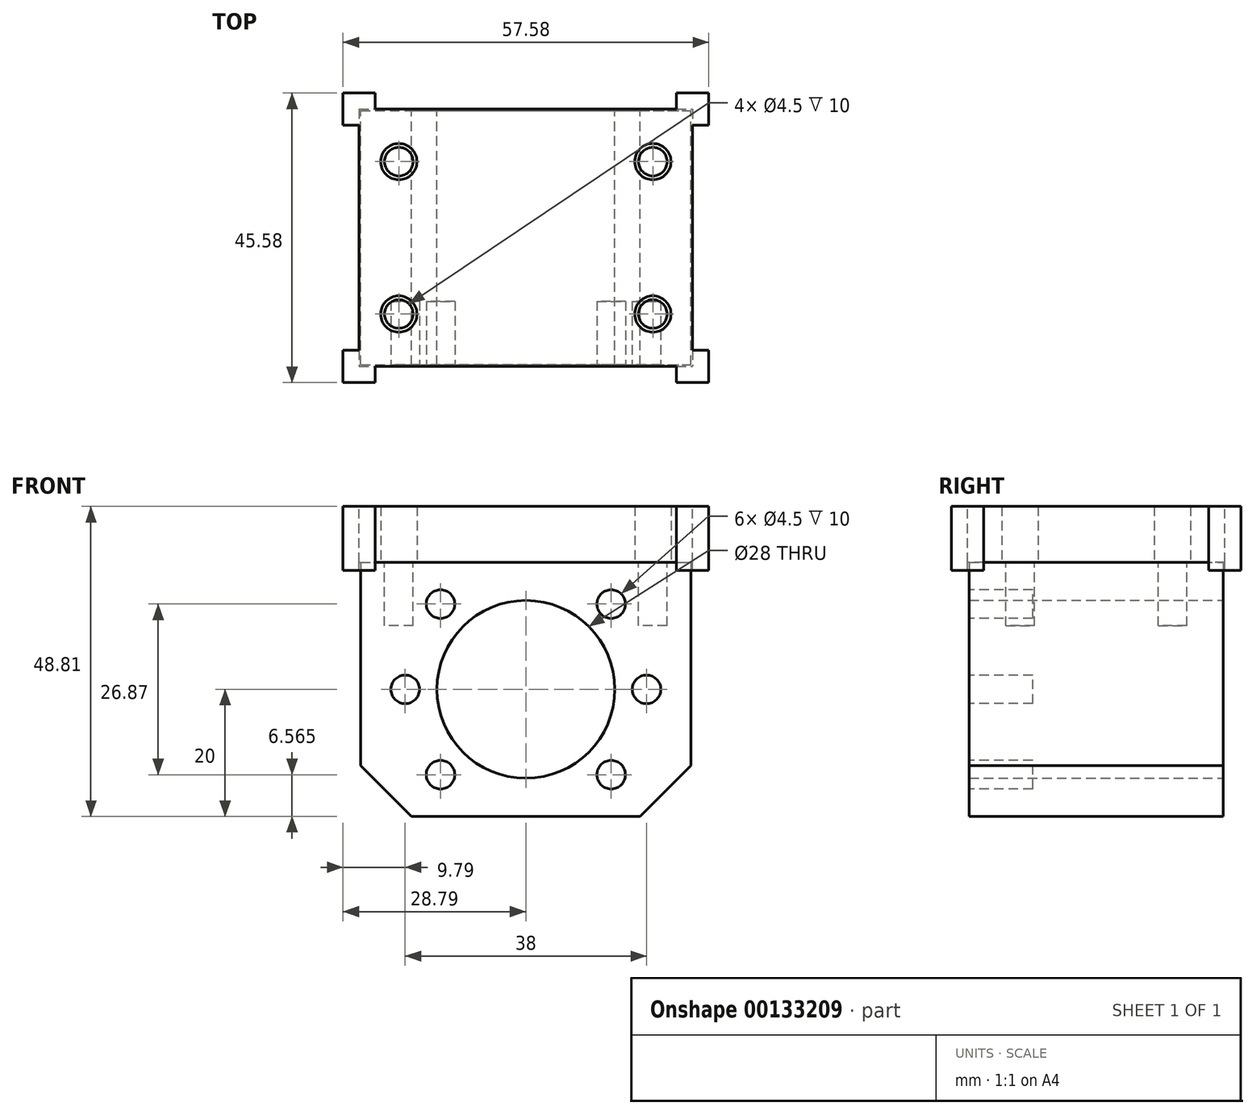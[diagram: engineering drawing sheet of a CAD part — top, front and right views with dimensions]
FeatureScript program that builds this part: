
annotation { "Feature Type Name" : "Feature", "Feature Type Description" : "" }
export const myFeature = defineFeature(function(context is Context, id is Id, definition is map)
    precondition{}
    {
        {
            var Q0;
            Q0=qCreatedBy(makeId("Front.planeOp"),FACE);
            var sketch = newSketch(context, id + "F0", { "sketchPlane" : qUnion([Q0])});
            skCircle(sketch, "E0", {"center": v(0, 0) * mm, "radius": 14 * mm});
            skLineSegment(sketch, "E1.bottom", {"start": v(-26, 20) * mm, "end": v(26, 20) * mm});
            skLineSegment(sketch, "E1.top", {"start": v(-18, -20) * mm, "end": v(18, -20) * mm});
            skLineSegment(sketch, "E1.left", {"start": v(-26, 20) * mm, "end": v(-26, -12) * mm});
            skLineSegment(sketch, "E1.right", {"start": v(26, 20) * mm, "end": v(26, -12) * mm});
            skLineSegment(sketch, "E2", {"start": v(-26, -12) * mm, "end": v(-18, -20) * mm});
            skLineSegment(sketch, "E3", {"start": v(18, -20) * mm, "end": v(26, -12) * mm});
            skSolve(sketch);
        }
        {
            var Q0;
            Q0 = qSketchRegion(id + "F0", true);
            extrude(context, id + "F1", {"entities" : qUnion([Q0]), "depth" : 40 * mm, "offsetDistance" : 25 * mm, "symmetric" : true});
        }
        {
            var Q0;
            Q0=makeQuery(id+"F1.opExtrude","SWEPT_FACE",FACE,{"disambiguationData":[OSD([sQuery(id+"F0.wireOp",EDGE,"E1.bottom")])]});
            var sketch = newSketch(context, id + "F2", { "sketchPlane" : qUnion([Q0])});
            skCircle(sketch, "E4", {"center": v(-20, 12) * mm, "radius": 2.25 * mm});
            skCircle(sketch, "E5", {"center": v(20, 12) * mm, "radius": 2.25 * mm});
            skCircle(sketch, "E6", {"center": v(20, -12) * mm, "radius": 2.25 * mm});
            skCircle(sketch, "E7", {"center": v(-20, -12) * mm, "radius": 2.25 * mm});
            skSolve(sketch);
        }
        {
            var Q0;
            Q0 = qSketchRegion(id + "F2", true);
            extrude(context, id + "F3", {"entities" : qUnion([Q0]), "operationType" : NewBodyOperationType.REMOVE, "oppositeDirection" : true, "depth" : 10 * mm, "offsetDistance" : 25 * mm});
        }
        {
            var Q0;
            Q0=makeQuery(id+"F1.opExtrude","CAP_FACE",FACE,{"disambiguationData":[OSD([sQuery(id+"F0.wireOp",EDGE,"E0"),sQuery(id+"F0.wireOp",EDGE,"E1.bottom"),sQuery(id+"F0.wireOp",EDGE,"E1.top"),sQuery(id+"F0.wireOp",EDGE,"E1.left"),sQuery(id+"F0.wireOp",EDGE,"E1.right"),sQuery(id+"F0.wireOp",EDGE,"E2"),sQuery(id+"F0.wireOp",EDGE,"E3")])],"isStart":false});
            var sketch = newSketch(context, id + "F4", { "sketchPlane" : qUnion([Q0])});
            skCircle(sketch, "E8", {"center": v(0, 0) * mm, "radius": 19 * mm, "construction": true});
            skCircle(sketch, "E9", {"center": v(-19, 0) * mm, "radius": 2.25 * mm});
            skCircle(sketch, "E10", {"center": v(19, 0) * mm, "radius": 2.25 * mm});
            skCircle(sketch, "E11", {"center": v(13.44, 13.44) * mm, "radius": 2.25 * mm});
            skCircle(sketch, "E12", {"center": v(-13.44, -13.44) * mm, "radius": 2.25 * mm});
            skCircle(sketch, "E13", {"center": v(-13.44, 13.44) * mm, "radius": 2.25 * mm});
            skCircle(sketch, "E14", {"center": v(13.44, -13.44) * mm, "radius": 2.25 * mm});
            skLineSegment(sketch, "E15", {"start": v(0, 0) * mm, "end": v(13.44, 13.44) * mm, "construction": true});
            skSolve(sketch);
        }
        {
            var Q0;
            Q0 = qSketchRegion(id + "F4", true);
            extrude(context, id + "F5", {"entities" : qUnion([Q0]), "operationType" : NewBodyOperationType.REMOVE, "oppositeDirection" : true, "depth" : 10 * mm, "offsetDistance" : 25 * mm});
        }
        {
            var Q0;
            Q0=makeQuery(id+"F1.opExtrude","SWEPT_FACE",FACE,{"disambiguationData":[OSD([sQuery(id+"F0.wireOp",EDGE,"E1.bottom")])]});
            var sketch = newSketch(context, id + "F6", { "sketchPlane" : qUnion([Q0])});
            skCircle(sketch, "E16", {"center": v(-20, 12) * mm, "radius": 2.86 * mm});
            skCircle(sketch, "E17", {"center": v(-20, -12) * mm, "radius": 2.86 * mm});
            skCircle(sketch, "E18", {"center": v(20, -12) * mm, "radius": 2.86 * mm});
            skCircle(sketch, "E19", {"center": v(20, 12) * mm, "radius": 2.86 * mm});
            skLineSegment(sketch, "E20.bottom", {"start": v(-26.25, 20.25) * mm, "end": v(26.25, 20.25) * mm});
            skLineSegment(sketch, "E20.top", {"start": v(-26.25, -20.25) * mm, "end": v(26.25, -20.25) * mm});
            skLineSegment(sketch, "E20.left", {"start": v(-26.25, 20.25) * mm, "end": v(-26.25, -20.25) * mm});
            skLineSegment(sketch, "E20.right", {"start": v(26.25, 20.25) * mm, "end": v(26.25, -20.25) * mm});
            skSolve(sketch);
        }
        {
            var Q0;
            Q0 = qSketchRegion(id + "F6", true);
            extrude(context, id + "F7", {"entities" : qUnion([Q0]), "depth" : 5 * mm, "offsetDistance" : 25.4 * mm});
        }
        {
            var Q0;
            Q0=makeQuery(id+"F7.opExtrude","CAP_FACE",FACE,{"disambiguationData":[OSD([sQuery(id+"F6.wireOp",EDGE,"E16"),sQuery(id+"F6.wireOp",EDGE,"E17"),sQuery(id+"F6.wireOp",EDGE,"E18"),sQuery(id+"F6.wireOp",EDGE,"E19"),sQuery(id+"F6.wireOp",EDGE,"E20.bottom"),sQuery(id+"F6.wireOp",EDGE,"E20.top"),sQuery(id+"F6.wireOp",EDGE,"E20.left"),sQuery(id+"F6.wireOp",EDGE,"E20.right")])],"isStart":false});
            var sketch = newSketch(context, id + "F8", { "sketchPlane" : qUnion([Q0])});
            skLineSegment(sketch, "E21", {"start": v(-26.25, 17.71) * mm, "end": v(-28.8, 17.71) * mm});
            skLineSegment(sketch, "E22", {"start": v(-28.8, 17.71) * mm, "end": v(-28.8, 22.8) * mm});
            skLineSegment(sketch, "E23", {"start": v(-28.8, 22.8) * mm, "end": v(-23.71, 22.8) * mm});
            skLineSegment(sketch, "E24", {"start": v(-23.71, 22.8) * mm, "end": v(-23.71, 20.25) * mm});
            skLineSegment(sketch, "E25", {"start": v(-23.71, 20.25) * mm, "end": v(-26.25, 20.25) * mm});
            skLineSegment(sketch, "E26", {"start": v(-26.25, 20.25) * mm, "end": v(-26.25, 17.71) * mm});
            skLineSegment(sketch, "E27", {"start": v(-28.8, -17.71) * mm, "end": v(-28.8, -22.8) * mm});
            skLineSegment(sketch, "E28", {"start": v(-28.8, -22.8) * mm, "end": v(-23.71, -22.8) * mm});
            skLineSegment(sketch, "E29", {"start": v(-23.71, -22.8) * mm, "end": v(-23.71, -20.25) * mm});
            skLineSegment(sketch, "E30", {"start": v(-23.71, -20.25) * mm, "end": v(-26.25, -20.25) * mm});
            skLineSegment(sketch, "E31", {"start": v(-26.25, -20.25) * mm, "end": v(-26.25, -17.71) * mm});
            skLineSegment(sketch, "E32", {"start": v(-26.25, -17.71) * mm, "end": v(-28.8, -17.71) * mm});
            skLineSegment(sketch, "E33", {"start": v(0, 0) * mm, "end": v(0, 29.08) * mm, "construction": true});
            skLineSegment(sketch, "E34.MirrorCS", {"start": v(26.25, 17.71) * mm, "end": v(28.8, 17.71) * mm});
            skLineSegment(sketch, "E35.MirrorCS", {"start": v(23.71, -20.25) * mm, "end": v(26.25, -20.25) * mm});
            skLineSegment(sketch, "E36.MirrorCS", {"start": v(23.71, -22.8) * mm, "end": v(23.71, -20.25) * mm});
            skLineSegment(sketch, "E37.MirrorCS", {"start": v(23.71, 20.25) * mm, "end": v(26.25, 20.25) * mm});
            skLineSegment(sketch, "E38.MirrorCS", {"start": v(26.25, -17.71) * mm, "end": v(28.8, -17.71) * mm});
            skLineSegment(sketch, "E39.MirrorCS", {"start": v(26.25, -20.25) * mm, "end": v(26.25, -17.71) * mm});
            skLineSegment(sketch, "E40.MirrorCS", {"start": v(26.25, 20.25) * mm, "end": v(26.25, 17.71) * mm});
            skLineSegment(sketch, "E41.MirrorCS", {"start": v(23.71, 22.8) * mm, "end": v(23.71, 20.25) * mm});
            skLineSegment(sketch, "E42.MirrorCS", {"start": v(28.8, 22.8) * mm, "end": v(23.71, 22.8) * mm});
            skLineSegment(sketch, "E43.MirrorCS", {"start": v(28.8, 17.71) * mm, "end": v(28.8, 22.8) * mm});
            skLineSegment(sketch, "E44.MirrorCS", {"start": v(28.8, -22.8) * mm, "end": v(23.71, -22.8) * mm});
            skLineSegment(sketch, "E45.MirrorCS", {"start": v(28.8, -17.71) * mm, "end": v(28.8, -22.8) * mm});
            skSolve(sketch);
        }
        {
            var Q0;
            Q0 = qSketchRegion(id + "F8", true);
            extrude(context, id + "F9", {"entities" : qUnion([Q0]), "operationType" : NewBodyOperationType.ADD, "oppositeDirection" : true, "depth" : 6.27 * mm, "offsetDistance" : 25.4 * mm});
        }
        {
            var Q0;
            {var subQ0=sQuery(id+"F6.wireOp",EDGE,"E20.top");var subQ1=sQuery(id+"F8.wireOp",EDGE,"E29");Q0=makeQuery(id+"F9.boolean.opBoolean","SPLIT",EDGE,{"disambiguationData":[topologyDisambiguationEdgeConnected([makeQuery(id+"F7.opExtrude","SWEPT_FACE",FACE,{"disambiguationData":[OSD([subQ0])]})])],"derivedFrom":makeQuery(id+"F9.opExtrude","SWEPT_EDGE",EDGE,{"disambiguationData":[OSD([subQ0,subQ1,sQuery(id+"F8.wireOp",EDGE,"E30")])]})});}
            var Q1;
            {var subQ0=sQuery(id+"F6.wireOp",EDGE,"E20.right");var subQ1=sQuery(id+"F8.wireOp",EDGE,"E38.MirrorCS");Q1=makeQuery(id+"F9.boolean.opBoolean","SPLIT",EDGE,{"disambiguationData":[topologyDisambiguationEdgeConnected([makeQuery(id+"F7.opExtrude","SWEPT_FACE",FACE,{"disambiguationData":[OSD([subQ0])]})])],"derivedFrom":makeQuery(id+"F9.opExtrude","SWEPT_EDGE",EDGE,{"disambiguationData":[OSD([subQ0,subQ1,sQuery(id+"F8.wireOp",EDGE,"E39.MirrorCS")])]})});}
            var Q2;
            {var subQ0=sQuery(id+"F6.wireOp",EDGE,"E20.bottom");var subQ1=sQuery(id+"F8.wireOp",EDGE,"E24");Q2=makeQuery(id+"F9.boolean.opBoolean","SPLIT",EDGE,{"disambiguationData":[topologyDisambiguationEdgeConnected([makeQuery(id+"F7.opExtrude","SWEPT_FACE",FACE,{"disambiguationData":[OSD([subQ0])]})])],"derivedFrom":makeQuery(id+"F9.opExtrude","SWEPT_EDGE",EDGE,{"disambiguationData":[OSD([subQ0,subQ1,sQuery(id+"F8.wireOp",EDGE,"E25")])]})});}
            var Q3;
            {var subQ0=sQuery(id+"F6.wireOp",EDGE,"E20.bottom");var subQ1=sQuery(id+"F8.wireOp",EDGE,"E41.MirrorCS");Q3=makeQuery(id+"F9.boolean.opBoolean","SPLIT",EDGE,{"disambiguationData":[topologyDisambiguationEdgeConnected([makeQuery(id+"F7.opExtrude","SWEPT_FACE",FACE,{"disambiguationData":[OSD([subQ0])]})])],"derivedFrom":makeQuery(id+"F9.opExtrude","SWEPT_EDGE",EDGE,{"disambiguationData":[OSD([subQ0,sQuery(id+"F8.wireOp",EDGE,"E37.MirrorCS"),subQ1])]})});}
            var Q4;
            {var subQ0=sQuery(id+"F6.wireOp",EDGE,"E20.left");var subQ1=sQuery(id+"F8.wireOp",EDGE,"E32");Q4=makeQuery(id+"F9.boolean.opBoolean","SPLIT",EDGE,{"disambiguationData":[topologyDisambiguationEdgeConnected([makeQuery(id+"F7.opExtrude","SWEPT_FACE",FACE,{"disambiguationData":[OSD([subQ0])]})])],"derivedFrom":makeQuery(id+"F9.opExtrude","SWEPT_EDGE",EDGE,{"disambiguationData":[OSD([subQ0,sQuery(id+"F8.wireOp",EDGE,"E31"),subQ1])]})});}
            var Q5;
            {var subQ0=sQuery(id+"F6.wireOp",EDGE,"E20.left");var subQ1=sQuery(id+"F8.wireOp",EDGE,"E21");Q5=makeQuery(id+"F9.boolean.opBoolean","SPLIT",EDGE,{"disambiguationData":[topologyDisambiguationEdgeConnected([makeQuery(id+"F7.opExtrude","SWEPT_FACE",FACE,{"disambiguationData":[OSD([subQ0])]})])],"derivedFrom":makeQuery(id+"F9.opExtrude","SWEPT_EDGE",EDGE,{"disambiguationData":[OSD([subQ0,subQ1,sQuery(id+"F8.wireOp",EDGE,"E26")])]})});}
            var Q6;
            {var subQ0=sQuery(id+"F6.wireOp",EDGE,"E20.top");var subQ1=sQuery(id+"F8.wireOp",EDGE,"E36.MirrorCS");Q6=makeQuery(id+"F9.boolean.opBoolean","SPLIT",EDGE,{"disambiguationData":[topologyDisambiguationEdgeConnected([makeQuery(id+"F7.opExtrude","SWEPT_FACE",FACE,{"disambiguationData":[OSD([subQ0])]})])],"derivedFrom":makeQuery(id+"F9.opExtrude","SWEPT_EDGE",EDGE,{"disambiguationData":[OSD([subQ0,sQuery(id+"F8.wireOp",EDGE,"E35.MirrorCS"),subQ1])]})});}
            var Q7;
            {var subQ0=sQuery(id+"F6.wireOp",EDGE,"E20.right");var subQ1=sQuery(id+"F8.wireOp",EDGE,"E34.MirrorCS");Q7=makeQuery(id+"F9.boolean.opBoolean","SPLIT",EDGE,{"disambiguationData":[topologyDisambiguationEdgeConnected([makeQuery(id+"F7.opExtrude","SWEPT_FACE",FACE,{"disambiguationData":[OSD([subQ0])]})])],"derivedFrom":makeQuery(id+"F9.opExtrude","SWEPT_EDGE",EDGE,{"disambiguationData":[OSD([subQ0,subQ1,sQuery(id+"F8.wireOp",EDGE,"E40.MirrorCS")])]})});}
            fillet(context, id + "F10", {"entities" : qUnion([Q0, Q1, Q2, Q3, Q4, Q5, Q6, Q7]), "radius" : 2.03 * mm, "tangentPropagation" : true, "allowEdgeOverflow" : false});
        }
        {
            var Q0;
            Q0=makeQuery(id+"F9.boolean.opBoolean","MERGE",FACE,{"derivedFrom":[makeQuery(id+"F7.opExtrude","CAP_FACE",FACE,{"disambiguationData":[OSD([sQuery(id+"F6.wireOp",EDGE,"E16"),sQuery(id+"F6.wireOp",EDGE,"E17"),sQuery(id+"F6.wireOp",EDGE,"E18"),sQuery(id+"F6.wireOp",EDGE,"E19"),sQuery(id+"F6.wireOp",EDGE,"E20.bottom"),sQuery(id+"F6.wireOp",EDGE,"E20.top"),sQuery(id+"F6.wireOp",EDGE,"E20.left"),sQuery(id+"F6.wireOp",EDGE,"E20.right")])],"isStart":false}),makeQuery(id+"F9.opExtrude","CAP_FACE",FACE,{"disambiguationData":[OSD([sQuery(id+"F8.wireOp",EDGE,"E21"),sQuery(id+"F8.wireOp",EDGE,"E22"),sQuery(id+"F8.wireOp",EDGE,"E23"),sQuery(id+"F8.wireOp",EDGE,"E24"),sQuery(id+"F8.wireOp",EDGE,"E25"),sQuery(id+"F8.wireOp",EDGE,"E26")])],"isStart":true}),makeQuery(id+"F9.opExtrude","CAP_FACE",FACE,{"disambiguationData":[OSD([sQuery(id+"F8.wireOp",EDGE,"E27"),sQuery(id+"F8.wireOp",EDGE,"E28"),sQuery(id+"F8.wireOp",EDGE,"E29"),sQuery(id+"F8.wireOp",EDGE,"E30"),sQuery(id+"F8.wireOp",EDGE,"E31"),sQuery(id+"F8.wireOp",EDGE,"E32")])],"isStart":true}),makeQuery(id+"F9.opExtrude","CAP_FACE",FACE,{"disambiguationData":[OSD([sQuery(id+"F8.wireOp",EDGE,"E34.MirrorCS"),sQuery(id+"F8.wireOp",EDGE,"E37.MirrorCS"),sQuery(id+"F8.wireOp",EDGE,"E40.MirrorCS"),sQuery(id+"F8.wireOp",EDGE,"E41.MirrorCS"),sQuery(id+"F8.wireOp",EDGE,"E42.MirrorCS"),sQuery(id+"F8.wireOp",EDGE,"E43.MirrorCS")])],"isStart":true}),makeQuery(id+"F9.opExtrude","CAP_FACE",FACE,{"disambiguationData":[OSD([sQuery(id+"F8.wireOp",EDGE,"E35.MirrorCS"),sQuery(id+"F8.wireOp",EDGE,"E36.MirrorCS"),sQuery(id+"F8.wireOp",EDGE,"E38.MirrorCS"),sQuery(id+"F8.wireOp",EDGE,"E39.MirrorCS"),sQuery(id+"F8.wireOp",EDGE,"E44.MirrorCS"),sQuery(id+"F8.wireOp",EDGE,"E45.MirrorCS")])],"isStart":true})]});
            var Q1;
            Q1=makeQuery(id+"F7.opExtrude","CAP_FACE",FACE,{"disambiguationData":[OSD([sQuery(id+"F6.wireOp",EDGE,"E16"),sQuery(id+"F6.wireOp",EDGE,"E17"),sQuery(id+"F6.wireOp",EDGE,"E18"),sQuery(id+"F6.wireOp",EDGE,"E19"),sQuery(id+"F6.wireOp",EDGE,"E20.bottom"),sQuery(id+"F6.wireOp",EDGE,"E20.top"),sQuery(id+"F6.wireOp",EDGE,"E20.left"),sQuery(id+"F6.wireOp",EDGE,"E20.right")])],"isStart":true});
            extrude(context, id + "F11", {"entities" : qUnion([Q0]), "endBound" : BoundingType.UP_TO_SURFACE, "oppositeDirection" : true, "depth" : 25.4 * mm, "endBoundEntityFace" : qUnion([Q1]), "offsetDistance" : 25.4 * mm, "hasSecondDirection" : true, "secondDirectionOppositeDirection" : false, "secondDirectionDepth" : 3.8 * mm});
        }
        {
            var Q0;
            Q0=makeQuery(id+"F11.opExtrude","CAP_FACE",FACE,{"disambiguationData":[OSD([sQuery(id+"F6.wireOp",EDGE,"E16"),sQuery(id+"F6.wireOp",EDGE,"E17"),sQuery(id+"F6.wireOp",EDGE,"E18"),sQuery(id+"F6.wireOp",EDGE,"E19"),sQuery(id+"F6.wireOp",EDGE,"E20.bottom"),sQuery(id+"F6.wireOp",EDGE,"E20.top"),sQuery(id+"F6.wireOp",EDGE,"E20.left"),sQuery(id+"F6.wireOp",EDGE,"E20.right"),sQuery(id+"F8.wireOp",EDGE,"E21"),sQuery(id+"F8.wireOp",EDGE,"E22"),sQuery(id+"F8.wireOp",EDGE,"E23"),sQuery(id+"F8.wireOp",EDGE,"E24"),sQuery(id+"F8.wireOp",EDGE,"E25"),sQuery(id+"F8.wireOp",EDGE,"E26"),sQuery(id+"F8.wireOp",EDGE,"E27"),sQuery(id+"F8.wireOp",EDGE,"E28"),sQuery(id+"F8.wireOp",EDGE,"E29"),sQuery(id+"F8.wireOp",EDGE,"E30"),sQuery(id+"F8.wireOp",EDGE,"E31"),sQuery(id+"F8.wireOp",EDGE,"E32"),sQuery(id+"F8.wireOp",EDGE,"E34.MirrorCS"),sQuery(id+"F8.wireOp",EDGE,"E35.MirrorCS"),sQuery(id+"F8.wireOp",EDGE,"E36.MirrorCS"),sQuery(id+"F8.wireOp",EDGE,"E37.MirrorCS"),sQuery(id+"F8.wireOp",EDGE,"E38.MirrorCS"),sQuery(id+"F8.wireOp",EDGE,"E39.MirrorCS"),sQuery(id+"F8.wireOp",EDGE,"E40.MirrorCS"),sQuery(id+"F8.wireOp",EDGE,"E41.MirrorCS"),sQuery(id+"F8.wireOp",EDGE,"E42.MirrorCS"),sQuery(id+"F8.wireOp",EDGE,"E43.MirrorCS"),sQuery(id+"F8.wireOp",EDGE,"E44.MirrorCS"),sQuery(id+"F8.wireOp",EDGE,"E45.MirrorCS")])],"isStart":false});
            var sketch = newSketch(context, id + "F12", { "sketchPlane" : qUnion([Q0])});
            skLineSegment(sketch, "E46.0", {"start": v(-28.8, 22.8) * mm, "end": v(-28.8, 17.71) * mm});
            skLineSegment(sketch, "E47.0", {"start": v(-23.71, 22.8) * mm, "end": v(-28.8, 22.8) * mm});
            skLineSegment(sketch, "E48.0", {"start": v(-23.71, 20.25) * mm, "end": v(-23.71, 22.8) * mm});
            skLineSegment(sketch, "E49.0", {"start": v(-23.71, -22.8) * mm, "end": v(-28.8, -22.8) * mm});
            skLineSegment(sketch, "E50.0", {"start": v(-28.8, -22.8) * mm, "end": v(-28.8, -17.71) * mm});
            skLineSegment(sketch, "E51.0", {"start": v(-23.71, -20.25) * mm, "end": v(-23.71, -22.8) * mm});
            skLineSegment(sketch, "E52.0", {"start": v(23.71, -22.8) * mm, "end": v(28.8, -22.8) * mm});
            skLineSegment(sketch, "E53.0", {"start": v(28.8, -17.71) * mm, "end": v(26.25, -17.71) * mm});
            skLineSegment(sketch, "E54.0", {"start": v(28.8, -22.8) * mm, "end": v(28.8, -17.71) * mm});
            skLineSegment(sketch, "E55.bottom", {"start": v(26.25, 17.71) * mm, "end": v(28.8, 17.71) * mm});
            skLineSegment(sketch, "E55.top", {"start": v(23.71, 22.8) * mm, "end": v(28.8, 22.8) * mm});
            skLineSegment(sketch, "E55.left", {"start": v(23.71, 20.25) * mm, "end": v(23.71, 22.8) * mm});
            skLineSegment(sketch, "E55.right", {"start": v(28.8, 17.71) * mm, "end": v(28.8, 22.8) * mm});
            skLineSegment(sketch, "E56", {"start": v(-28.8, 17.71) * mm, "end": v(-26.25, 17.71) * mm});
            skLineSegment(sketch, "E57", {"start": v(-26.25, 17.71) * mm, "end": v(-26.25, 20.25) * mm});
            skLineSegment(sketch, "E58", {"start": v(-26.25, 20.25) * mm, "end": v(-23.71, 20.25) * mm});
            skLineSegment(sketch, "E59", {"start": v(-26.25, -17.71) * mm, "end": v(-26.25, -20.25) * mm});
            skLineSegment(sketch, "E60", {"start": v(-26.25, -20.25) * mm, "end": v(-23.71, -20.25) * mm});
            skPoint(sketch, "E61.orphan", {"position": v(-23.71, -22.29) * mm});
            skLineSegment(sketch, "E62", {"start": v(-28.8, -17.71) * mm, "end": v(-26.25, -17.71) * mm});
            skLineSegment(sketch, "E63", {"start": v(23.71, -22.8) * mm, "end": v(23.71, -20.25) * mm});
            skLineSegment(sketch, "E64", {"start": v(23.71, -20.25) * mm, "end": v(26.25, -20.25) * mm});
            skLineSegment(sketch, "E65", {"start": v(26.25, -20.25) * mm, "end": v(26.25, -17.71) * mm});
            skPoint(sketch, "E66.orphan", {"position": v(23.71, -17.71) * mm});
            skLineSegment(sketch, "E67", {"start": v(23.71, 20.25) * mm, "end": v(26.25, 20.25) * mm});
            skLineSegment(sketch, "E68", {"start": v(26.25, 20.25) * mm, "end": v(26.25, 17.71) * mm});
            skSolve(sketch);
        }
        {
            var Q0;
            Q0 = qSketchRegion(id + "F12", true);
            extrude(context, id + "F13", {"entities" : qUnion([Q0]), "operationType" : NewBodyOperationType.ADD, "depth" : 1.27 * mm, "offsetDistance" : 25.4 * mm});
        }
    });
